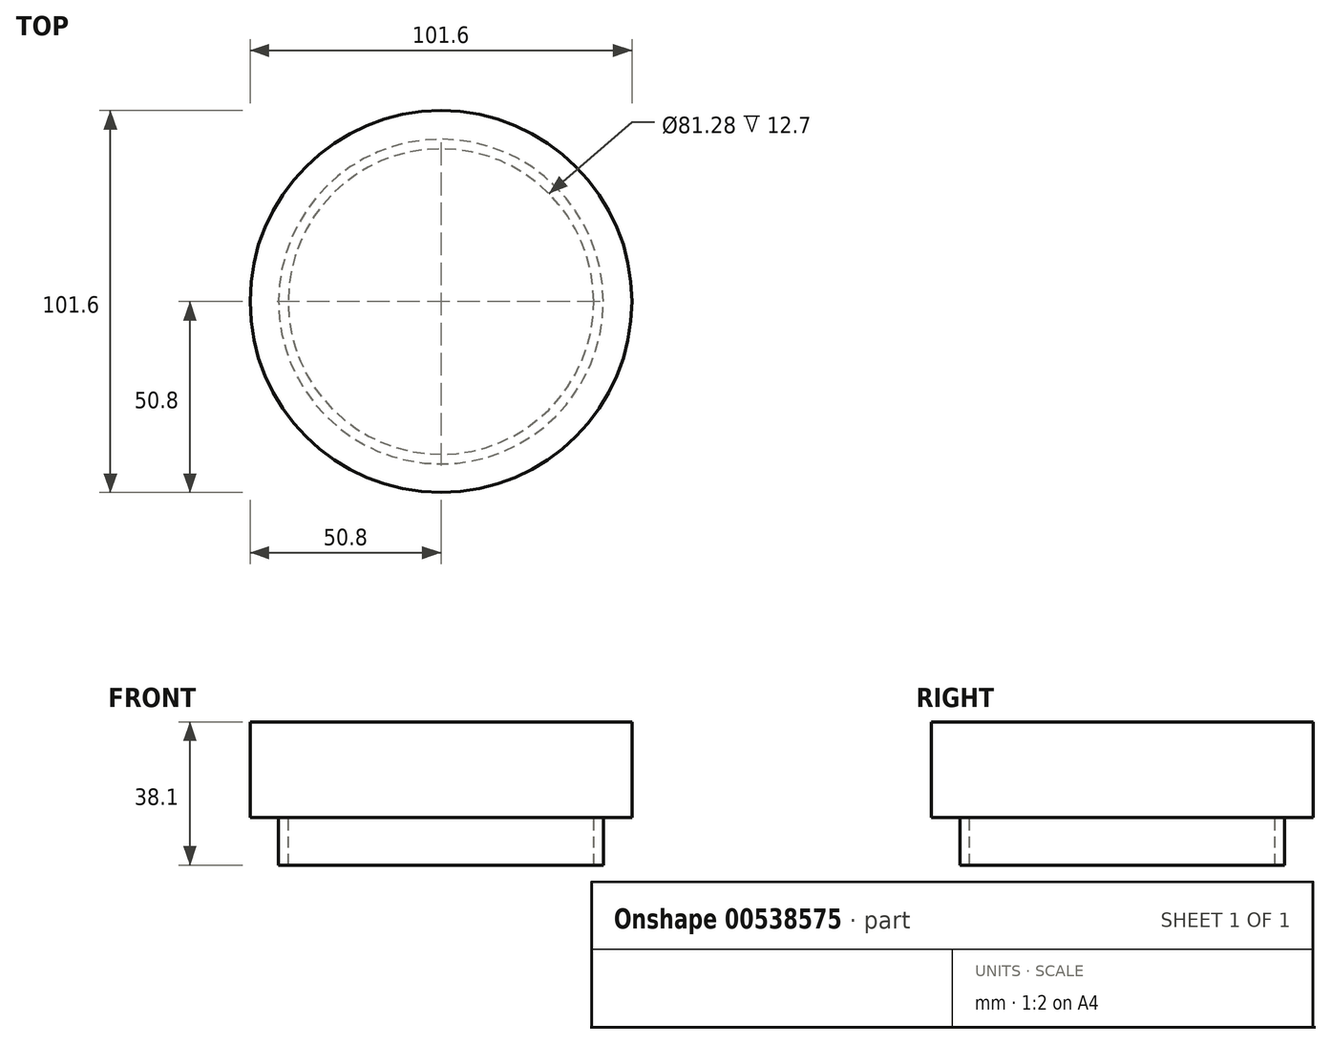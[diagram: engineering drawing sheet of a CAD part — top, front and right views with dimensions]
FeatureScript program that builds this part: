
annotation { "Feature Type Name" : "Feature", "Feature Type Description" : "" }
export const myFeature = defineFeature(function(context is Context, id is Id, definition is map)
    precondition{}
    {
        {
            var Q0;
            Q0=qCreatedBy(makeId("Top.planeOp"),FACE);
            var sketch = newSketch(context, id + "F0", { "sketchPlane" : qUnion([Q0])});
            skCircle(sketch, "E0", {"center": v(0, 0) * mm, "radius": 50.8 * mm});
            skSolve(sketch);
        }
        {
            var Q0;
            Q0=makeQuery(id+"F0.imprint","IMPRINT",FACE,{"disambiguationData":[TD([[makeQuery(id+"F0.imprint","IMPRINT",EDGE,{"derivedFrom":sQuery(id+"F0.wireOp",EDGE,"E0")}),1.0]])]});
            extrude(context, id + "F1", {"entities" : qUnion([Q0]), "depth" : 25.4 * mm, "offsetDistance" : 25.4 * mm});
        }
        {
            var Q0;
            Q0=makeQuery(id+"F1.opExtrude","CAP_FACE",FACE,{"disambiguationData":[OSD([sQuery(id+"F0.wireOp",EDGE,"E0")])],"isStart":true});
            var sketch = newSketch(context, id + "F2", { "sketchPlane" : qUnion([Q0])});
            skCircle(sketch, "E1", {"center": v(0, 0) * mm, "radius": 43.18 * mm});
            skCircle(sketch, "E2", {"center": v(0, 0) * mm, "radius": 40.64 * mm});
            skSolve(sketch);
        }
        {
            var Q0;
            Q0=makeQuery(id+"F2.imprint","IMPRINT",FACE,{"disambiguationData":[TD([[makeQuery(id+"F2.imprint","IMPRINT",EDGE,{"derivedFrom":sQuery(id+"F2.wireOp",EDGE,"E1")}),1.0]])]});
            extrude(context, id + "F3", {"entities" : qUnion([Q0]), "operationType" : NewBodyOperationType.ADD, "depth" : 12.7 * mm, "offsetDistance" : 25.4 * mm});
        }
    });
